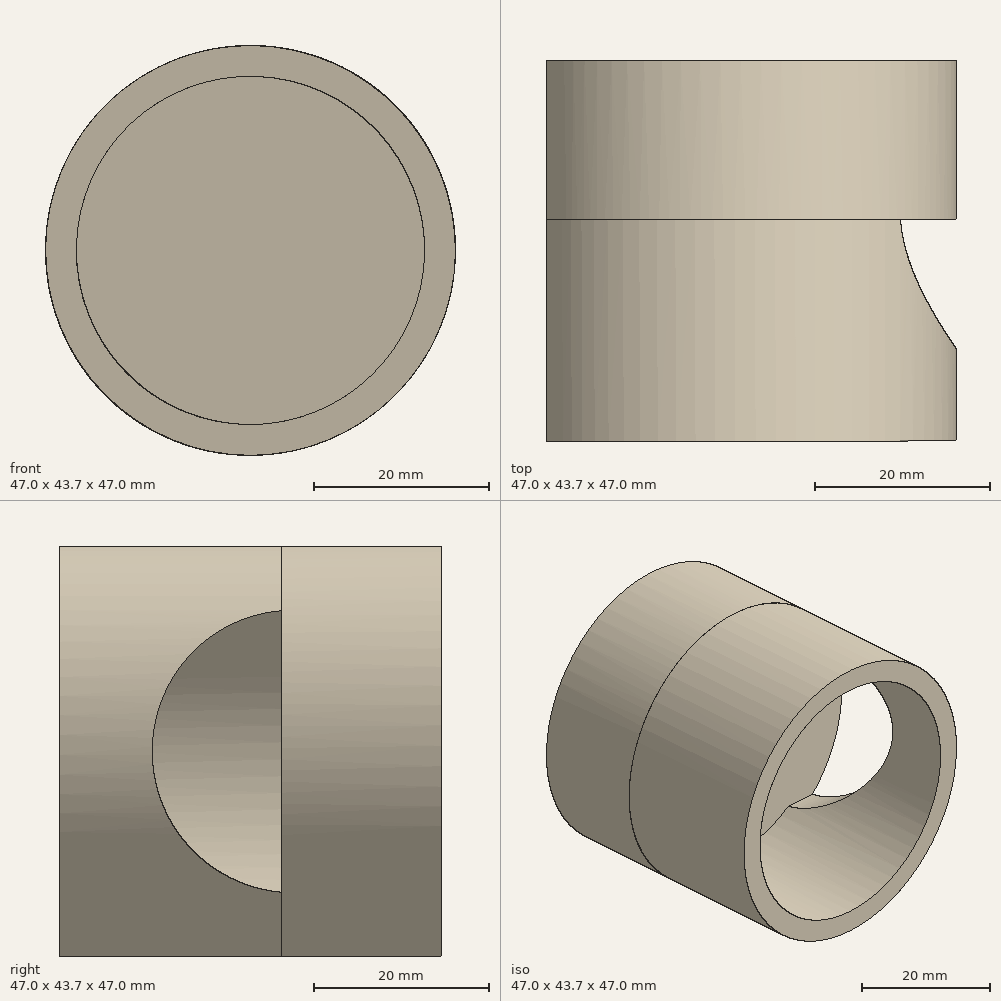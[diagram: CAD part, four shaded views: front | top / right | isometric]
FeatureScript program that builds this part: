
annotation { "Feature Type Name" : "Feature", "Feature Type Description" : "" }
export const myFeature = defineFeature(function(context is Context, id is Id, definition is map)
    precondition{}
    {
        {
            var Q0;
            Q0=qCreatedBy(makeId("Front.planeOp"),FACE);
            var sketch = newSketch(context, id + "F0", { "sketchPlane" : qUnion([Q0])});
            skCircle(sketch, "E0", {"center": v(0, 0) * mm, "radius": 23.5 * mm});
            skSolve(sketch);
        }
        {
            var Q0;
            Q0 = qSketchRegion(id + "F0", true);
            extrude(context, id + "F1", {"entities" : qUnion([Q0]), "depth" : 25.4 * mm, "offsetDistance" : 25.4 * mm});
        }
        {
            var Q0;
            Q0=qCreatedBy(makeId("Front.planeOp"),FACE);
            var sketch = newSketch(context, id + "F2", { "sketchPlane" : qUnion([Q0])});
            skCircle(sketch, "E1", {"center": v(0, 0) * mm, "radius": 19.97 * mm});
            skSolve(sketch);
        }
        {
            var Q0;
            Q0 = qSketchRegion(id + "F2", true);
            extrude(context, id + "F3", {"entities" : qUnion([Q0]), "operationType" : NewBodyOperationType.REMOVE, "depth" : 27.18 * mm, "offsetDistance" : 25.4 * mm});
        }
        {
            var Q0;
            Q0=qCreatedBy(makeId("Right.planeOp"),FACE);
            var sketch = newSketch(context, id + "F4", { "sketchPlane" : qUnion([Q0])});
            skCircle(sketch, "E2", {"center": v(1.38, 0) * mm, "radius": 16.2 * mm});
            skSolve(sketch);
        }
        {
            var Q0;
            Q0 = qSketchRegion(id + "F4", true);
            extrude(context, id + "F5", {"entities" : qUnion([Q0]), "operationType" : NewBodyOperationType.REMOVE, "depth" : 37.85 * mm, "offsetDistance" : 25.4 * mm});
        }
        {
            var Q0;
            Q0=qCreatedBy(makeId("Front.planeOp"),FACE);
            var sketch = newSketch(context, id + "F6", { "sketchPlane" : qUnion([Q0])});
            skCircle(sketch, "E3", {"center": v(0, 0) * mm, "radius": 23.51 * mm});
            skSolve(sketch);
        }
        {
            var Q0;
            Q0 = qSketchRegion(id + "F6", true);
            extrude(context, id + "F7", {"entities" : qUnion([Q0]), "operationType" : NewBodyOperationType.ADD, "oppositeDirection" : true, "depth" : 18.29 * mm, "offsetDistance" : 25.4 * mm});
        }
    });
